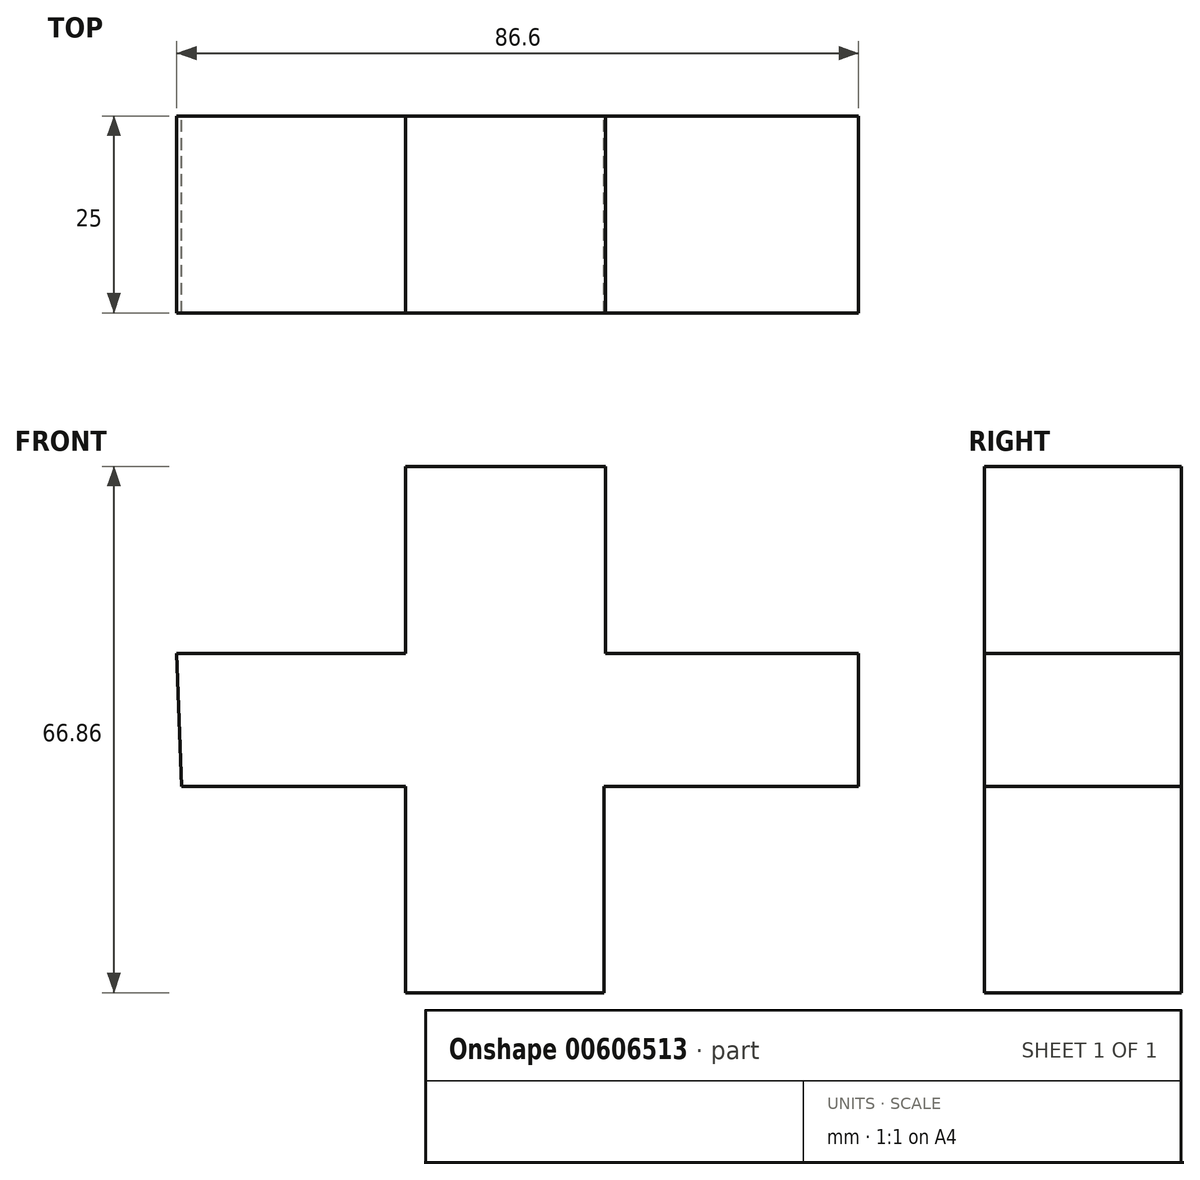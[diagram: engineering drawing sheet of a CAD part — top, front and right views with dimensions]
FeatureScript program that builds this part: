
annotation { "Feature Type Name" : "Feature", "Feature Type Description" : "" }
export const myFeature = defineFeature(function(context is Context, id is Id, definition is map)
    precondition{}
    {
        {
            var Q0;
            Q0=qCreatedBy(makeId("Front.planeOp"),FACE);
            var sketch = newSketch(context, id + "F0", { "sketchPlane" : qUnion([Q0])});
            skLineSegment(sketch, "E0", {"start": v(-50.8, 6.07) * mm, "end": v(-21.77, 6.07) * mm});
            skLineSegment(sketch, "E1", {"start": v(-21.77, 6.07) * mm, "end": v(-21.77, 29.86) * mm});
            skLineSegment(sketch, "E2", {"start": v(3.69, 29.86) * mm, "end": v(3.69, 6.07) * mm});
            skLineSegment(sketch, "E3", {"start": v(3.69, 6.07) * mm, "end": v(35.8, 6.07) * mm});
            skLineSegment(sketch, "E4", {"start": v(35.8, 6.07) * mm, "end": v(35.8, -10.27) * mm});
            skLineSegment(sketch, "E5", {"start": v(3.45, -10.83) * mm, "end": v(3.45, -37) * mm});
            skLineSegment(sketch, "E6", {"start": v(3.45, -37) * mm, "end": v(-21.77, -37) * mm});
            skLineSegment(sketch, "E7", {"start": v(-21.77, -37) * mm, "end": v(-21.77, -10.83) * mm});
            skLineSegment(sketch, "E8", {"start": v(-21.77, -10.83) * mm, "end": v(-50.2, -10.83) * mm});
            skLineSegment(sketch, "E9", {"start": v(-50.2, -10.83) * mm, "end": v(-50.8, 6.07) * mm});
            skLineSegment(sketch, "E10", {"start": v(-21.77, 29.86) * mm, "end": v(3.69, 29.86) * mm});
            skLineSegment(sketch, "E11", {"start": v(3.45, -10.83) * mm, "end": v(35.8, -10.83) * mm});
            skLineSegment(sketch, "E12", {"start": v(35.8, -10.27) * mm, "end": v(35.8, -10.83) * mm});
            skSolve(sketch);
        }
        {
            var Q0;
            Q0 = qSketchRegion(id + "F0", true);
            extrude(context, id + "F1", {"entities" : qUnion([Q0]), "depth" : 25 * mm, "offsetDistance" : 25 * mm});
        }
    });
